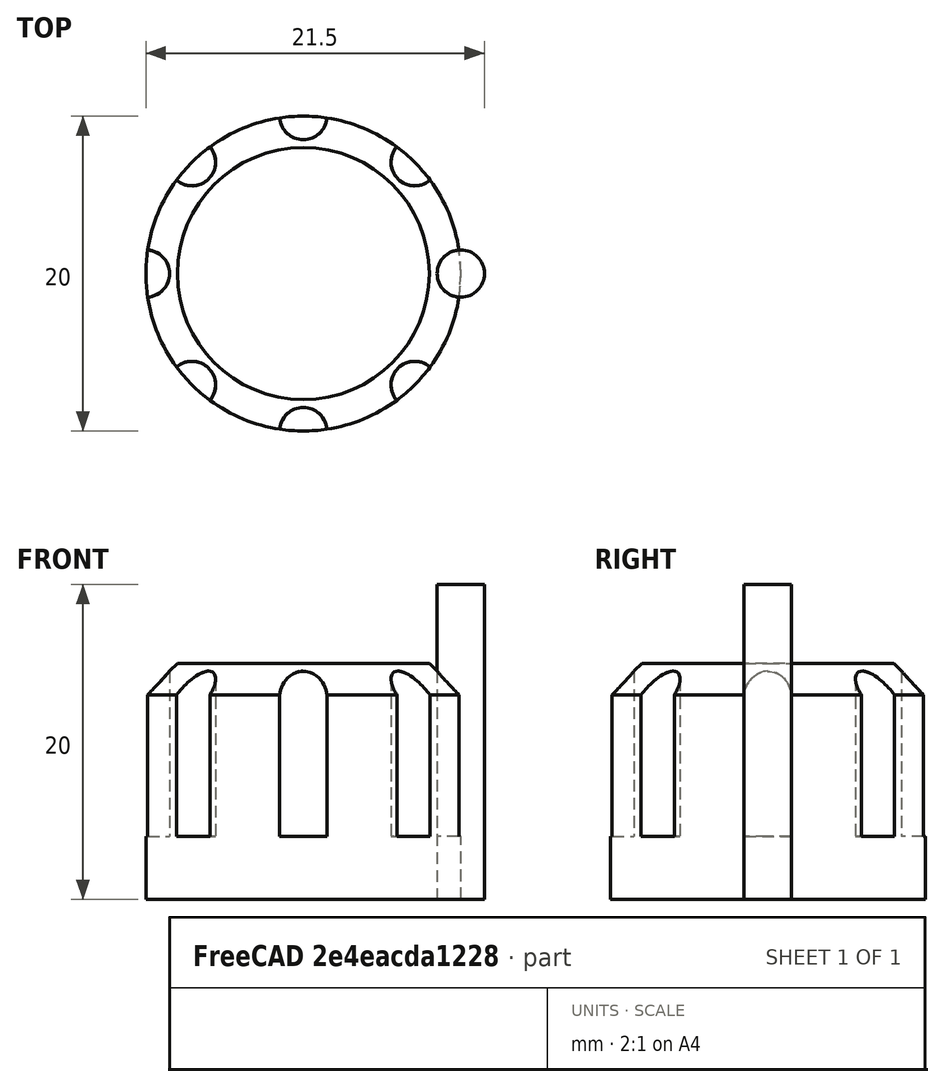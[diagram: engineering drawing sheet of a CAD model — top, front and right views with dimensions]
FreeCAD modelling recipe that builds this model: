
FCSTD DOCUMENT  (FreeCAD 0.21R33694 (Git))
Label: OJT1_T12P01.tapD'ampolla
License: All rights reserved
LicenseURL: http://en.wikipedia.org/wiki/All_rights_reserved
objects: Part::Cylinder×2, Part::FeaturePython×1, Part::Chamfer×1, Part::Cut×1
note: 4 computed .brp shape members not serialized (recipe doc carries the construction recipe); baked Part::Feature solids carry a one-line shape summary decoded from their .brp

FEATURE [Part::Cylinder] Cylinder  label="Cilindre"
  Angle = 360
  AttacherType = Attacher::AttachEngine3D
  FirstAngle = 0
  Height = 15
  Radius = 10
  SecondAngle = 0
FEATURE [Part::Cylinder] Cylinder001  label="Cilindre001"
  Angle = 360
  AttacherType = Attacher::AttachEngine3D
  FirstAngle = 0
  Height = 20
  Placement = pos=(10,0,0) rot=(0,0,1;0rad)
  Radius = 1.5
  SecondAngle = 0
FEATURE [Part::FeaturePython] Array  # Draft array (typed FeaturePython)
  AlwaysSyncPlacement = false
  Angle = 360
  ArrayType = 1
  Axis = (0,0,1)
  Base = -> Cylinder001
  Center = (0,0,0)
  Count = 8
  ExpandArray = false
  Fuse = false
  IntervalAxis = (0,0,0)
  IntervalX = (50,0,0)
  IntervalY = (0,50,0)
  IntervalZ = (0,0,50)
  NumberCircles = 3
  NumberPolar = 8
  NumberX = 2
  NumberY = 2
  NumberZ = 1
  Placement = pos=(0,0,4) rot=(0,0,1;0rad)
  PlacementList = 8 placements: [(10,0,0),(7.07107,7.07107,0),(0,10,0),(-7.07107,7.07107,0),(-10,1.22465e-15,0),(-7.07107,-7.07107,0),(-2.22045e-15,-10,0),(7.07107,-7.07107,0)]
  RadialDistance = 50
  ScaleList = (8) [(1,1,1),(1,1,1),(1,1,1),(1,1,1),(1,1,1),(1,1,1),(1,1,1),(1,1,1)]
  Symmetry = 1
  TangentialDistance = 25
FEATURE [Part::Chamfer] Chamfer
  Base = -> Cylinder
  Edges = 1 edges r=2: [Edge3]
FEATURE [Part::Cut] Cut
  Base = -> Chamfer
  Refine = true
  Tool = -> Array
